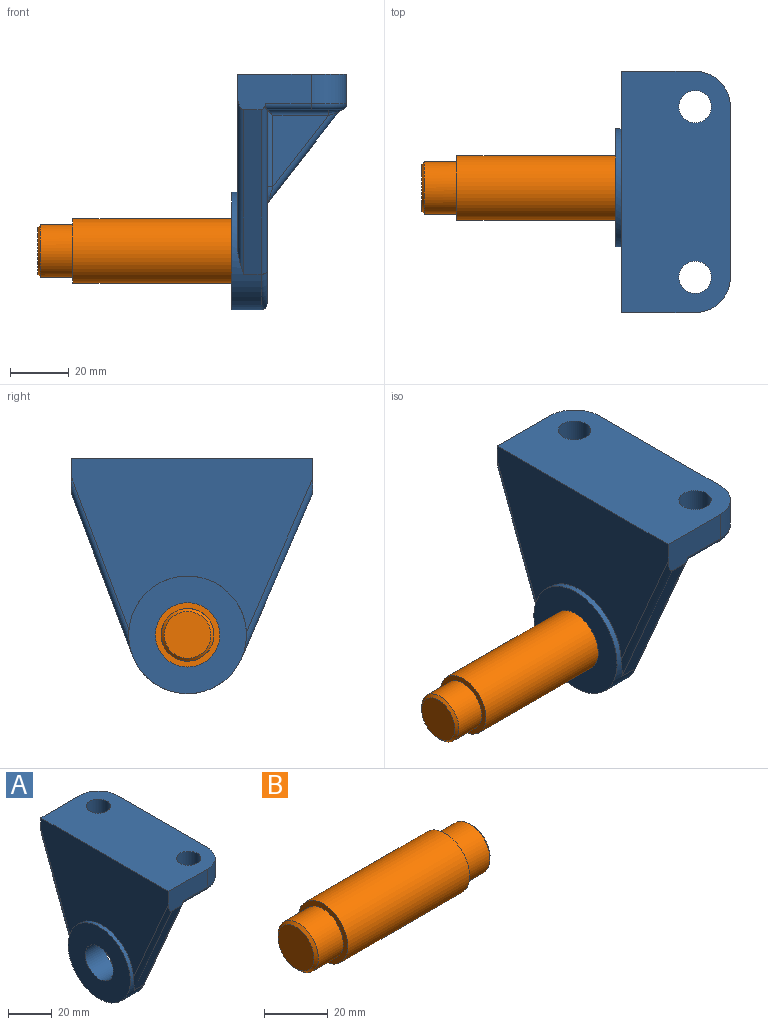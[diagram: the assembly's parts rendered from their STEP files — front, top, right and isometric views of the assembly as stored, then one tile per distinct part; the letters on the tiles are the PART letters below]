
ASSEMBLY  parts=2 mates=1
PART A: 50 faces, bbox 42.2x87.9x83.9 mm
  f0: plane 28.13x25mm, normal (0,0,-1), area 388.2mm2, adj f1,f17,f26,f29,f42,f43,f44,f47
  f1: plane 77.68x66mm, normal (1,0,0), area 2349.8mm2, adj f0,f2,f6,f24,f25,f28,f30,f33
  f2: plane 31.16x25.01mm, normal (0,0,-1), area 463.9mm2, adj f1,f19,f34,f35,f36,f37,f38,f45
  f3: plane 55.93x24.15mm, normal (0,-0.92,-0.4), area 365.5mm2, adj f4,f9,f45,f49
  f4: cylinder r=20mm len=40mm, axis (1,0,0), area 649.1mm2, adj f3,f5,f7,f8,f46,f48,f49
  f5: plane 55.06x20.77mm, normal (0,0.94,-0.35), area 353.1mm2, adj f4,f13,f47,f48
  f6: cylinder r=9mm len=18mm, axis (1,0,0), area 678.6mm2, adj f1,f8
  f7: plane 82x59.13mm, normal (-1,0,0), area 3141.7mm2, adj f4,f9,f13,f16,f48,f49
  f8: plane 40x40mm, normal (-1,0,0), area 1002.2mm2, adj f4,f6
  f9: plane 26.95x13.95mm, normal (0,-1,0), area 266.1mm2, adj f3,f7,f10,f16,f36,f45,f49
  f10: cylinder r=12mm len=12mm, axis (0,0,-1), area 188.5mm2, adj f9,f11,f16,f37
  f11: plane 58x10.12mm, normal (1,0,0), area 582mm2, adj f10,f12,f16,f38,f39,f40,f41,f42
  f12: cylinder r=12mm len=12mm, axis (0,0,-1), area 188.5mm2, adj f11,f13,f16,f43
  f13: plane 27.23x14.23mm, normal (0,1,0), area 265.7mm2, adj f5,f7,f12,f16,f44,f47,f48
  f14: cylinder r=5.5mm len=11mm, axis (0,0,-1), area 345.6mm2, adj f16,f20
  f15: cylinder r=5.5mm len=11mm, axis (0,0,-1), area 345.6mm2, adj f16,f18
  f16: plane 82x37mm, normal (0,0,1), area 2782.1mm2, adj f7,f9,f10,f11,f12,f13,f14,f15
  f17: cylinder r=9mm len=18mm, axis (0,0,-1), area 113.1mm2, adj f0,f18
  f18: plane 18x18mm, normal (0,0,-1), area 159.4mm2, adj f15,f17
  f19: cylinder r=9mm len=18mm, axis (0,0,-1), area 113.1mm2, adj f2,f20
  f20: plane 18x18mm, normal (0,0,-1), area 159.4mm2, adj f14,f19
  f21: plane 30.69x23.98mm, normal (0.79,0,-0.62), area 545.2mm2, adj f27,f28,f31,f32
  f22: plane 24.19x18.9mm, normal (0,-1,0), area 228.6mm2, adj f32,f33,f35
  f23: plane 24.19x18.9mm, normal (0,1,0), area 228.6mm2, adj f24,f26,f27
  f24: cylinder r=2mm len=26.19mm, axis (0,0,-1), area 79.1mm2, adj f1,f23,f25,f26
  f25: bspline ~6.5x4mm, area 15.2mm2, adj f1,f24,f27,f28
  f26: cylinder r=2mm len=20.9mm, axis (-1,0,0), area 62.5mm2, adj f0,f23,f24,f29
  f27: cylinder r=2mm len=31.92mm, axis (0.62,0,0.79), area 109.4mm2, adj f21,f23,f25,f29
  f28: cylinder r=2mm len=14mm, axis (0,1,0), area 18.6mm2, adj f1,f21,f25,f30
  f29: bspline ~5.08x4mm, area 12.6mm2, adj f0,f26,f27,f31,f41
  f30: bspline ~6.5x4mm, area 15.2mm2, adj f1,f28,f32,f33
  f31: cylinder r=2mm len=14mm, axis (0,-1,0), area 18.5mm2, adj f21,f29,f34,f40
  f32: cylinder r=2mm len=31.92mm, axis (-0.62,0,-0.79), area 109.4mm2, adj f21,f22,f30,f34
  f33: cylinder r=2mm len=26.19mm, axis (0,0,1), area 79.1mm2, adj f1,f22,f30,f35
  f34: bspline ~5.08x4mm, area 12.6mm2, adj f2,f31,f32,f35,f39
  f35: cylinder r=2mm len=20.9mm, axis (1,0,0), area 62.5mm2, adj f2,f22,f33,f34
  f36: cylinder r=2mm len=15.41mm, axis (1,0,0), area 47.8mm2, adj f2,f9,f37,f45
  f37: torus R=10mm, axis (0,0,1), area 55.6mm2, adj f2,f10,f36,f38
  f38: cylinder r=2mm len=21.16mm, axis (0,1,0), area 66.5mm2, adj f2,f11,f37,f39
  f39: bspline ~5.02x2.39mm, area 6.7mm2, adj f11,f34,f38,f40
  f40: cylinder r=2mm len=14mm, axis (0,-1,0), area 37.1mm2, adj f11,f31,f39,f41
  f41: bspline ~3.11x2.15mm, area 6.7mm2, adj f11,f29,f40,f42
  f42: cylinder r=2mm len=18.13mm, axis (0,1,0), area 57mm2, adj f0,f11,f41,f43
  f43: torus R=10mm, axis (0,0,1), area 55.6mm2, adj f0,f12,f42,f44
  f44: cylinder r=2mm len=15.48mm, axis (-1,0,0), area 47.9mm2, adj f0,f13,f43,f47
  f45: cylinder r=2mm len=58.41mm, axis (0,0.4,-0.92), area 191.8mm2, adj f1,f2,f3,f9,f36,f46
  f46: torus R=18mm, axis (1,0,0), area 143.7mm2, adj f1,f4,f45,f47
  f47: cylinder r=2mm len=57.52mm, axis (0,0.35,0.94), area 185.4mm2, adj f0,f1,f5,f13,f44,f46
  f48: cylinder r=2mm len=60.73mm, axis (0,-0.35,-0.94), area 179.5mm2, adj f4,f5,f7,f13
  f49: cylinder r=2mm len=60.97mm, axis (0,-0.4,0.92), area 185mm2, adj f3,f4,f7,f9
PART B: 9 faces, bbox 78x21.9x21.9 mm
  f0: cylinder r=10.95mm len=54mm, axis (-1,0,0), area 3715.2mm2, adj f1,f2
  f1: plane 21.9x21.9mm, normal (1,0,0), area 125mm2, adj f0,f3
  f2: plane 21.9x21.9mm, normal (-1,0,0), area 125mm2, adj f0,f6
  f3: cylinder r=8.95mm len=17.9mm, axis (-1,0,0), area 618.6mm2, adj f1,f5
  f4: plane 15.9x15.9mm, normal (1,0,0), area 198.6mm2, adj f5
  f5: cone r=7.95mm half-angle=45deg, axis (-1,0,0), area 75.1mm2, adj f3,f4
  f6: cylinder r=8.95mm len=17.9mm, axis (1,0,0), area 618.6mm2, adj f2,f8
  f7: plane 15.9x15.9mm, normal (-1,0,0), area 198.6mm2, adj f8
  f8: cone r=7.95mm half-angle=45deg, axis (1,0,0), area 75.1mm2, adj f6,f7
PLACE A at identity
PLACE B t=(-39,0,0)mm
MATE cylindrical B.f3 <-> A.f4  axis (1,0,0) through (0,0,0)mm
